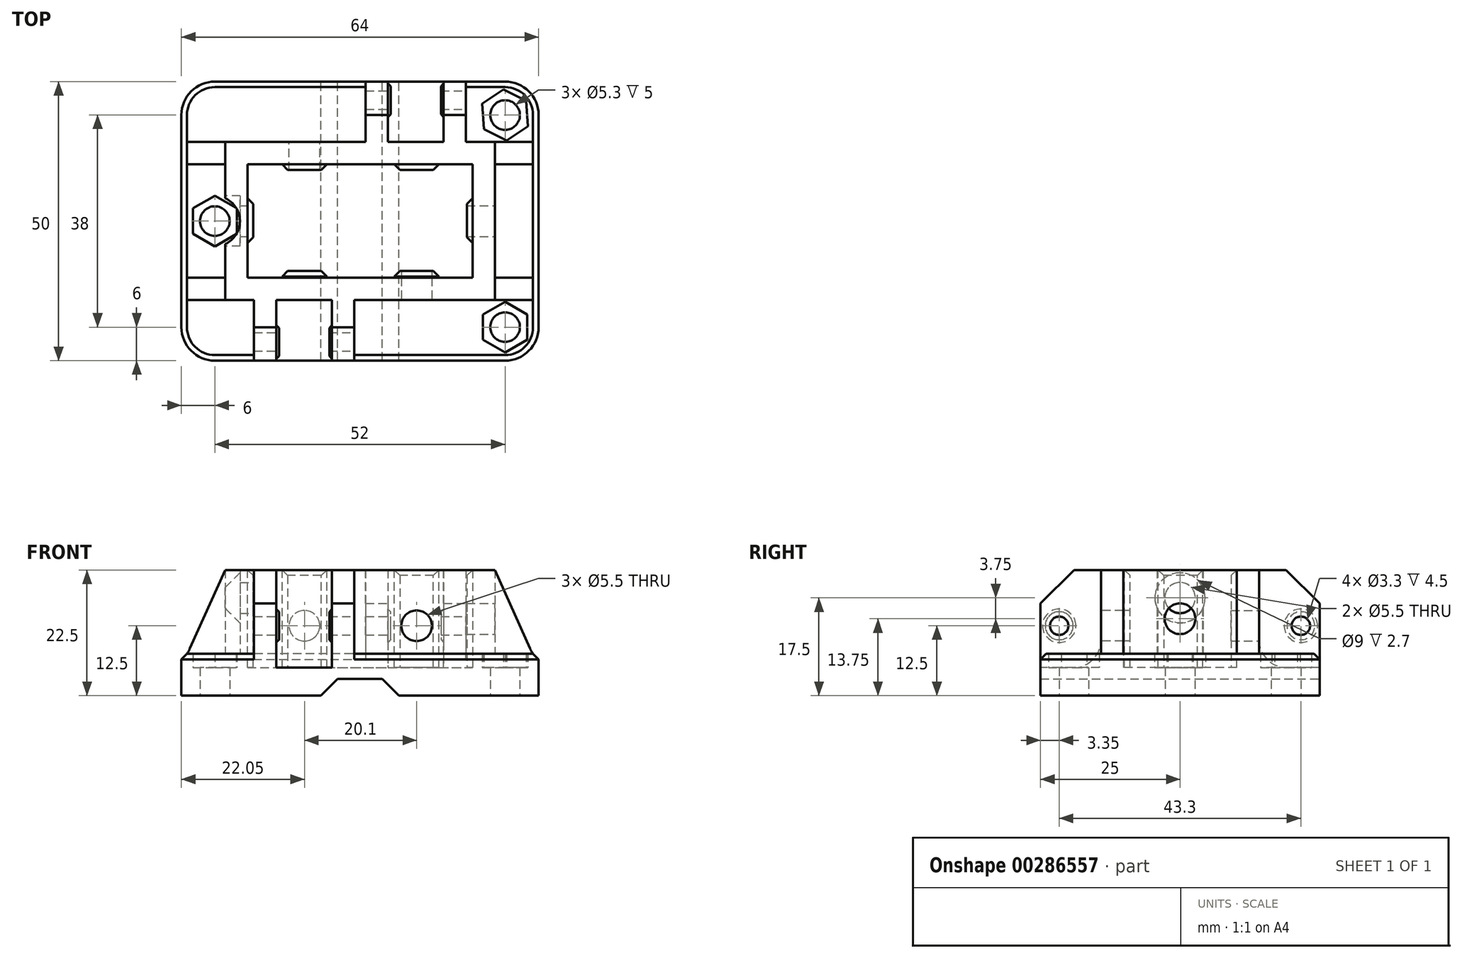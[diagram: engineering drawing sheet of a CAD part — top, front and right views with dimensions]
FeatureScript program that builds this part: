
annotation { "Feature Type Name" : "Feature", "Feature Type Description" : "" }
export const myFeature = defineFeature(function(context is Context, id is Id, definition is map)
    precondition{}
    {
        {
            var Q0;
            Q0=qCreatedBy(makeId("Top.planeOp"),FACE);
            var sketch = newSketch(context, id + "F0", { "sketchPlane" : qUnion([Q0])});
            skLineSegment(sketch, "E0.bottom", {"start": v(0, 0) * mm, "end": v(64, 0) * mm});
            skLineSegment(sketch, "E0.top", {"start": v(0, 50) * mm, "end": v(64, 50) * mm});
            skLineSegment(sketch, "E0.left", {"start": v(0, 0) * mm, "end": v(0, 50) * mm});
            skLineSegment(sketch, "E0.right", {"start": v(64, 0) * mm, "end": v(64, 50) * mm});
            skCircle(sketch, "E1", {"center": v(58, 44) * mm, "radius": 2.65 * mm});
            skPoint(sketch, "E2.centerSnap0", {"position": v(32, 0) * mm});
            skCircle(sketch, "E3", {"center": v(58, 6) * mm, "radius": 2.65 * mm});
            skCircle(sketch, "E4", {"center": v(6, 25) * mm, "radius": 2.65 * mm});
            skPoint(sketch, "E4.centerSnap0", {"position": v(0, 25) * mm});
            skSolve(sketch);
        }
        {
            var Q0;
            Q0 = qSketchRegion(id + "F0", true);
            extrude(context, id + "F1", {"entities" : qUnion([Q0]), "depth" : 5 * mm});
        }
        {
            var Q0;
            Q0=makeQuery(id+"F1.opExtrude","CAP_FACE",FACE,{"disambiguationData":[OSD([sQuery(id+"F0.wireOp",EDGE,"E0.bottom"),sQuery(id+"F0.wireOp",EDGE,"E0.top"),sQuery(id+"F0.wireOp",EDGE,"E0.left"),sQuery(id+"F0.wireOp",EDGE,"E0.right"),sQuery(id+"F0.wireOp",EDGE,"SUFVuphh-Qgx9-THfo-SX6n-8QSMb4j17lpz"),sQuery(id+"F0.wireOp",EDGE,"E1"),sQuery(id+"F0.wireOp",EDGE,"E2")])],"isStart":false});
            var sketch = newSketch(context, id + "F2", { "sketchPlane" : qUnion([Q0])});
            skLineSegment(sketch, "E5.bottom", {"start": v(7.85, 39.15) * mm, "end": v(56.15, 39.15) * mm});
            skLineSegment(sketch, "E5.top", {"start": v(7.85, 10.85) * mm, "end": v(56.15, 10.85) * mm});
            skLineSegment(sketch, "E5.left", {"start": v(7.85, 39.15) * mm, "end": v(7.85, 29.1) * mm});
            skLineSegment(sketch, "E5.right", {"start": v(56.15, 39.15) * mm, "end": v(56.15, 10.85) * mm});
            skLineSegment(sketch, "E6.0.0", {"start": v(64, 50) * mm, "end": v(0, 50) * mm, "construction": true});
            skLineSegment(sketch, "E6.0.1", {"start": v(0, 50) * mm, "end": v(0, 0) * mm, "construction": true});
            skLineSegment(sketch, "E6.0.2", {"start": v(0, 0) * mm, "end": v(64, 0) * mm, "construction": true});
            skLineSegment(sketch, "E6.0.3", {"start": v(64, 0) * mm, "end": v(64, 50) * mm, "construction": true});
            skArc(sketch, "E7", {"start": v(7.85, 20.9) * mm, "mid": v(10.5, 25) * mm, "end": v(7.85, 29.1) * mm});
            skLineSegment(sketch, "E8.trimOffspring", {"start": v(7.85, 20.9) * mm, "end": v(7.85, 10.85) * mm});
            skLineSegment(sketch, "E9.bottom", {"start": v(11.85, 35.15) * mm, "end": v(52.15, 35.15) * mm});
            skLineSegment(sketch, "E9.top", {"start": v(11.85, 14.85) * mm, "end": v(52.15, 14.85) * mm});
            skLineSegment(sketch, "E9.left", {"start": v(11.85, 35.15) * mm, "end": v(11.85, 14.85) * mm});
            skLineSegment(sketch, "E9.right", {"start": v(52.15, 35.15) * mm, "end": v(52.15, 14.85) * mm});
            skSolve(sketch);
        }
        {
            var Q0;
            Q0 = qSketchRegion(id + "F2", true);
            extrude(context, id + "F3", {"entities" : qUnion([Q0]), "operationType" : NewBodyOperationType.ADD, "depth" : 17.5 * mm});
        }
        {
            var Q0;
            Q0=makeQuery(id+"F3.opExtrude","CAP_FACE",FACE,{"disambiguationData":[OSD([sQuery(id+"F2.wireOp",EDGE,"E5.bottom"),sQuery(id+"F2.wireOp",EDGE,"E5.top"),sQuery(id+"F2.wireOp",EDGE,"E5.left"),sQuery(id+"F2.wireOp",EDGE,"E5.right"),sQuery(id+"F2.wireOp",EDGE,"E7"),sQuery(id+"F2.wireOp",EDGE,"E8.trimOffspring"),sQuery(id+"F2.wireOp",EDGE,"E9.bottom"),sQuery(id+"F2.wireOp",EDGE,"E9.top"),sQuery(id+"F2.wireOp",EDGE,"E9.left"),sQuery(id+"F2.wireOp",EDGE,"E9.right")])],"isStart":false});
            var sketch = newSketch(context, id + "F4", { "sketchPlane" : qUnion([Q0])});
            skLineSegment(sketch, "E10.bottom", {"start": v(11.85, 29.1) * mm, "end": v(12.85, 29.1) * mm});
            skLineSegment(sketch, "E10.top", {"start": v(11.85, 21.1) * mm, "end": v(12.85, 21.1) * mm});
            skLineSegment(sketch, "E10.left", {"start": v(11.85, 29.1) * mm, "end": v(11.85, 21.1) * mm});
            skLineSegment(sketch, "E10.right", {"start": v(12.85, 29.1) * mm, "end": v(12.85, 21.1) * mm});
            skLineSegment(sketch, "E11", {"start": v(32, 35.15) * mm, "end": v(32, 14.85) * mm, "construction": true});
            skLineSegment(sketch, "E12.MirrorCS", {"start": v(52.15, 29.1) * mm, "end": v(51.15, 29.1) * mm});
            skLineSegment(sketch, "E13.MirrorCS", {"start": v(52.15, 21.1) * mm, "end": v(51.15, 21.1) * mm});
            skLineSegment(sketch, "E14.MirrorCS", {"start": v(51.15, 29.1) * mm, "end": v(51.15, 21.1) * mm});
            skLineSegment(sketch, "E15.MirrorCS", {"start": v(52.15, 29.1) * mm, "end": v(52.15, 21.1) * mm});
            skLineSegment(sketch, "E16.bottom", {"start": v(38.15, 35.15) * mm, "end": v(46.15, 35.15) * mm});
            skLineSegment(sketch, "E16.top", {"start": v(38.15, 34.15) * mm, "end": v(46.15, 34.15) * mm});
            skLineSegment(sketch, "E16.left", {"start": v(38.15, 35.15) * mm, "end": v(38.15, 34.15) * mm});
            skLineSegment(sketch, "E16.right", {"start": v(46.15, 35.15) * mm, "end": v(46.15, 34.15) * mm});
            skLineSegment(sketch, "E17.bottom", {"start": v(18.05, 35.15) * mm, "end": v(26.05, 35.15) * mm});
            skLineSegment(sketch, "E17.top", {"start": v(18.05, 34.15) * mm, "end": v(26.05, 34.15) * mm});
            skLineSegment(sketch, "E17.left", {"start": v(18.05, 35.15) * mm, "end": v(18.05, 34.15) * mm});
            skLineSegment(sketch, "E17.right", {"start": v(26.05, 35.15) * mm, "end": v(26.05, 34.15) * mm});
            skLineSegment(sketch, "E18", {"start": v(52.15, 25.1) * mm, "end": v(11.85, 25.1) * mm, "construction": true});
            skLineSegment(sketch, "E19.MirrorCS", {"start": v(38.15, 15.05) * mm, "end": v(38.15, 16.05) * mm});
            skLineSegment(sketch, "E20.MirrorCS", {"start": v(18.05, 15.05) * mm, "end": v(18.05, 16.05) * mm});
            skLineSegment(sketch, "E21.MirrorCS", {"start": v(26.05, 15.05) * mm, "end": v(26.05, 16.05) * mm});
            skLineSegment(sketch, "E22.MirrorCS", {"start": v(46.15, 15.05) * mm, "end": v(46.15, 16.05) * mm});
            skLineSegment(sketch, "E23.MirrorCS", {"start": v(38.15, 15.05) * mm, "end": v(46.15, 15.05) * mm});
            skLineSegment(sketch, "E24.MirrorCS", {"start": v(18.05, 16.05) * mm, "end": v(26.05, 16.05) * mm});
            skLineSegment(sketch, "E25.MirrorCS", {"start": v(18.05, 15.05) * mm, "end": v(26.05, 15.05) * mm});
            skLineSegment(sketch, "E26.MirrorCS", {"start": v(38.15, 16.05) * mm, "end": v(46.15, 16.05) * mm});
            skSolve(sketch);
        }
        {
            var Q0;
            Q0 = qSketchRegion(id + "F4", true);
            var Q1;
            Q1=makeQuery(id+"F3.boolean.opBoolean","SPLIT",FACE,{"disambiguationData":[TD([makeQuery(id+"F3.opExtrude","SWEPT_FACE",FACE,{"disambiguationData":[OSD([sQuery(id+"F2.wireOp",EDGE,"E9.bottom")])]})])],"derivedFrom":makeQuery(id+"F1.opExtrude","CAP_FACE",FACE,{"disambiguationData":[OSD([sQuery(id+"F0.wireOp",EDGE,"E0.bottom"),sQuery(id+"F0.wireOp",EDGE,"E0.top"),sQuery(id+"F0.wireOp",EDGE,"E0.left"),sQuery(id+"F0.wireOp",EDGE,"E0.right"),sQuery(id+"F0.wireOp",EDGE,"E1"),sQuery(id+"F0.wireOp",EDGE,"E3"),sQuery(id+"F0.wireOp",EDGE,"E4")])],"isStart":false})});
            extrude(context, id + "F5", {"entities" : qUnion([Q0]), "operationType" : NewBodyOperationType.ADD, "endBound" : BoundingType.UP_TO_SURFACE, "oppositeDirection" : true, "endBoundEntityFace" : qUnion([Q1]), "depth" : 25 * mm});
        }
        {
            var Q0;
            Q0=makeQuery(id+"F5.opExtrude","SWEPT_EDGE",EDGE,{"disambiguationData":[OSD([sQuery(id+"F4.wireOp",EDGE,"E10.bottom"),sQuery(id+"F4.wireOp",EDGE,"E10.right")])]});
            var Q1;
            Q1=makeQuery(id+"F5.opExtrude","SWEPT_EDGE",EDGE,{"disambiguationData":[OSD([sQuery(id+"F4.wireOp",EDGE,"E10.top"),sQuery(id+"F4.wireOp",EDGE,"E10.right")])]});
            var Q2;
            Q2=makeQuery(id+"F5.opExtrude","CAP_EDGE",EDGE,{"disambiguationData":[OSD([sQuery(id+"F4.wireOp",EDGE,"E10.right")])],"isStart":true});
            var Q3;
            Q3=makeQuery(id+"F5.opExtrude","SWEPT_EDGE",EDGE,{"disambiguationData":[OSD([sQuery(id+"F4.wireOp",EDGE,"E12.MirrorCS"),sQuery(id+"F4.wireOp",EDGE,"E14.MirrorCS")])]});
            var Q4;
            Q4=makeQuery(id+"F5.opExtrude","SWEPT_EDGE",EDGE,{"disambiguationData":[OSD([sQuery(id+"F4.wireOp",EDGE,"E13.MirrorCS"),sQuery(id+"F4.wireOp",EDGE,"E14.MirrorCS")])]});
            var Q5;
            Q5=makeQuery(id+"F5.opExtrude","CAP_EDGE",EDGE,{"disambiguationData":[OSD([sQuery(id+"F4.wireOp",EDGE,"E14.MirrorCS")])],"isStart":true});
            var Q6;
            Q6=makeQuery(id+"F5.opExtrude","SWEPT_EDGE",EDGE,{"disambiguationData":[OSD([sQuery(id+"F4.wireOp",EDGE,"E17.top"),sQuery(id+"F4.wireOp",EDGE,"E17.left")])]});
            var Q7;
            Q7=makeQuery(id+"F5.opExtrude","CAP_EDGE",EDGE,{"disambiguationData":[OSD([sQuery(id+"F4.wireOp",EDGE,"E17.top")])],"isStart":true});
            var Q8;
            Q8=makeQuery(id+"F5.opExtrude","SWEPT_EDGE",EDGE,{"disambiguationData":[OSD([sQuery(id+"F4.wireOp",EDGE,"E17.top"),sQuery(id+"F4.wireOp",EDGE,"E17.right")])]});
            var Q9;
            Q9=makeQuery(id+"F5.opExtrude","SWEPT_EDGE",EDGE,{"disambiguationData":[OSD([sQuery(id+"F4.wireOp",EDGE,"E16.top"),sQuery(id+"F4.wireOp",EDGE,"E16.left")])]});
            var Q10;
            Q10=makeQuery(id+"F5.opExtrude","CAP_EDGE",EDGE,{"disambiguationData":[OSD([sQuery(id+"F4.wireOp",EDGE,"E16.top")])],"isStart":true});
            var Q11;
            Q11=makeQuery(id+"F5.opExtrude","SWEPT_EDGE",EDGE,{"disambiguationData":[OSD([sQuery(id+"F4.wireOp",EDGE,"E16.top"),sQuery(id+"F4.wireOp",EDGE,"E16.right")])]});
            var Q12;
            Q12=makeQuery(id+"F5.opExtrude","CAP_EDGE",EDGE,{"disambiguationData":[OSD([sQuery(id+"F4.wireOp",EDGE,"E26.MirrorCS")])],"isStart":true});
            var Q13;
            Q13=makeQuery(id+"F5.opExtrude","CAP_EDGE",EDGE,{"disambiguationData":[OSD([sQuery(id+"F4.wireOp",EDGE,"E24.MirrorCS")])],"isStart":true});
            var Q14;
            Q14=makeQuery(id+"F5.opExtrude","SWEPT_EDGE",EDGE,{"disambiguationData":[OSD([sQuery(id+"F4.wireOp",EDGE,"E20.MirrorCS"),sQuery(id+"F4.wireOp",EDGE,"E24.MirrorCS")])]});
            var Q15;
            Q15=makeQuery(id+"F5.opExtrude","SWEPT_EDGE",EDGE,{"disambiguationData":[OSD([sQuery(id+"F4.wireOp",EDGE,"E21.MirrorCS"),sQuery(id+"F4.wireOp",EDGE,"E24.MirrorCS")])]});
            var Q16;
            Q16=makeQuery(id+"F5.opExtrude","SWEPT_EDGE",EDGE,{"disambiguationData":[OSD([sQuery(id+"F4.wireOp",EDGE,"E19.MirrorCS"),sQuery(id+"F4.wireOp",EDGE,"E26.MirrorCS")])]});
            var Q17;
            Q17=makeQuery(id+"F5.opExtrude","SWEPT_EDGE",EDGE,{"disambiguationData":[OSD([sQuery(id+"F4.wireOp",EDGE,"E22.MirrorCS"),sQuery(id+"F4.wireOp",EDGE,"E26.MirrorCS")])]});
            chamfer(context, id + "F6", {"entities" : qUnion([Q0, Q1, Q2, Q3, Q4, Q5, Q6, Q7, Q8, Q9, Q10, Q11, Q12, Q13, Q14, Q15, Q16, Q17]), "width" : 1 * mm, "tangentPropagation" : true});
        }
        {
            var Q0;
            Q0=makeQuery(id+"F1.opExtrude","SWEPT_EDGE",EDGE,{"disambiguationData":[OSD([sQuery(id+"F0.wireOp",EDGE,"E0.bottom"),sQuery(id+"F0.wireOp",EDGE,"E0.right")])]});
            var Q1;
            Q1=makeQuery(id+"F1.opExtrude","SWEPT_EDGE",EDGE,{"disambiguationData":[OSD([sQuery(id+"F0.wireOp",EDGE,"E0.top"),sQuery(id+"F0.wireOp",EDGE,"E0.left")])]});
            var Q2;
            Q2=makeQuery(id+"F1.opExtrude","SWEPT_EDGE",EDGE,{"disambiguationData":[OSD([sQuery(id+"F0.wireOp",EDGE,"E0.top"),sQuery(id+"F0.wireOp",EDGE,"E0.right")])]});
            var Q3;
            Q3=makeQuery(id+"F1.opExtrude","SWEPT_EDGE",EDGE,{"disambiguationData":[OSD([sQuery(id+"F0.wireOp",EDGE,"E0.bottom"),sQuery(id+"F0.wireOp",EDGE,"E0.left")])]});
            fillet(context, id + "F7", {"entities" : qUnion([Q0, Q1, Q2, Q3]), "radius" : 6 * mm, "tangentPropagation" : true, "allowEdgeOverflow" : false});
        }
        {
            var Q0;
            {var subQ0=sQuery(id+"F0.wireOp",EDGE,"E0.left");var subQ1=sQuery(id+"F0.wireOp",EDGE,"E4");var subQ2=sQuery(id+"F0.wireOp",EDGE,"E3");var subQ3=sQuery(id+"F0.wireOp",EDGE,"E1");var subQ4=sQuery(id+"F0.wireOp",EDGE,"E0.bottom");var subQ5=sQuery(id+"F0.wireOp",EDGE,"E0.right");var subQ6=sQuery(id+"F0.wireOp",EDGE,"E0.top");Q0=makeQuery(id+"F3.boolean.opBoolean","SPLIT",FACE,{"disambiguationData":[TD([makeQuery(id+"F1.opExtrude","SWEPT_FACE",FACE,{"disambiguationData":[OSD([subQ4])]})])],"derivedFrom":makeQuery(id+"F1.opExtrude","CAP_FACE",FACE,{"disambiguationData":[OSD([subQ4,subQ6,subQ0,subQ5,subQ3,subQ2,subQ1])],"isStart":false})});}
            var sketch = newSketch(context, id + "F8", { "sketchPlane" : qUnion([Q0])});
            skLineSegment(sketch, "E27.bottom", {"start": v(7.85, 39.15) * mm, "end": v(0, 39.15) * mm});
            skLineSegment(sketch, "E27.top", {"start": v(7.85, 35.15) * mm, "end": v(0, 35.15) * mm});
            skLineSegment(sketch, "E27.left", {"start": v(7.85, 39.15) * mm, "end": v(7.85, 35.15) * mm});
            skLineSegment(sketch, "E27.right", {"start": v(0, 39.15) * mm, "end": v(0, 35.15) * mm});
            skLineSegment(sketch, "E28.bottom", {"start": v(7.85, 10.85) * mm, "end": v(0, 10.85) * mm});
            skLineSegment(sketch, "E28.top", {"start": v(7.85, 14.85) * mm, "end": v(0, 14.85) * mm});
            skLineSegment(sketch, "E28.left", {"start": v(7.85, 10.85) * mm, "end": v(7.85, 14.85) * mm});
            skLineSegment(sketch, "E28.right", {"start": v(0, 10.85) * mm, "end": v(0, 14.85) * mm});
            skLineSegment(sketch, "E29.bottom", {"start": v(56.15, 39.15) * mm, "end": v(64, 39.15) * mm});
            skLineSegment(sketch, "E29.top", {"start": v(56.15, 35.15) * mm, "end": v(64, 35.15) * mm});
            skLineSegment(sketch, "E29.left", {"start": v(56.15, 39.15) * mm, "end": v(56.15, 35.15) * mm});
            skLineSegment(sketch, "E29.right", {"start": v(64, 39.15) * mm, "end": v(64, 35.15) * mm});
            skLineSegment(sketch, "E30.bottom", {"start": v(56.15, 10.85) * mm, "end": v(64, 10.85) * mm});
            skLineSegment(sketch, "E30.top", {"start": v(56.15, 14.85) * mm, "end": v(64, 14.85) * mm});
            skLineSegment(sketch, "E30.left", {"start": v(56.15, 10.85) * mm, "end": v(56.15, 14.85) * mm});
            skLineSegment(sketch, "E30.right", {"start": v(64, 10.85) * mm, "end": v(64, 14.85) * mm});
            skLineSegment(sketch, "E31.bottom", {"start": v(7.85, 10.85) * mm, "end": v(12.5, 10.85) * mm});
            skLineSegment(sketch, "E32.bottom", {"start": v(7.85, 39.15) * mm, "end": v(12.5, 39.15) * mm});
            skLineSegment(sketch, "E33.0.0", {"start": v(7.85, 20.9) * mm, "end": v(7.85, 10.85) * mm, "construction": true});
            skLineSegment(sketch, "E33.0.1", {"start": v(12.5, 10.85) * mm, "end": v(48.25, 10.85) * mm, "construction": true});
            skLineSegment(sketch, "E33.0.2", {"start": v(56.15, 10.85) * mm, "end": v(56.15, 39.15) * mm, "construction": true});
            skLineSegment(sketch, "E33.0.3", {"start": v(56.15, 39.15) * mm, "end": v(12.5, 39.15) * mm, "construction": true});
            skLineSegment(sketch, "E33.0.4", {"start": v(7.85, 39.15) * mm, "end": v(7.85, 29.1) * mm, "construction": true});
            skArc(sketch, "E33.0.5", {"start": v(7.85, 29.1) * mm, "mid": v(10.5, 25) * mm, "end": v(7.85, 20.9) * mm, "construction": true});
            skLineSegment(sketch, "E34.0", {"start": v(52.15, 35.15) * mm, "end": v(52.15, 29.1) * mm, "construction": true});
            skLineSegment(sketch, "E35.0", {"start": v(52.15, 21.1) * mm, "end": v(52.15, 14.85) * mm, "construction": true});
            skLineSegment(sketch, "E36.bottom", {"start": v(51, 39.15) * mm, "end": v(47, 39.15) * mm});
            skLineSegment(sketch, "E36.top", {"start": v(51, 50) * mm, "end": v(47, 50) * mm});
            skLineSegment(sketch, "E36.left", {"start": v(51, 39.15) * mm, "end": v(51, 50) * mm});
            skLineSegment(sketch, "E36.right", {"start": v(47, 39.15) * mm, "end": v(47, 50) * mm});
            skLineSegment(sketch, "E37.bottom", {"start": v(37, 50) * mm, "end": v(33, 50) * mm});
            skLineSegment(sketch, "E37.top", {"start": v(37, 39.15) * mm, "end": v(33, 39.15) * mm});
            skLineSegment(sketch, "E37.left", {"start": v(37, 50) * mm, "end": v(37, 39.15) * mm});
            skLineSegment(sketch, "E37.right", {"start": v(33, 50) * mm, "end": v(33, 39.15) * mm});
            skLineSegment(sketch, "E38.bottom", {"start": v(27, 10.85) * mm, "end": v(31, 10.85) * mm});
            skLineSegment(sketch, "E38.top", {"start": v(27, 0) * mm, "end": v(31, 0) * mm});
            skLineSegment(sketch, "E38.left", {"start": v(27, 10.85) * mm, "end": v(27, 0) * mm});
            skLineSegment(sketch, "E38.right", {"start": v(31, 10.85) * mm, "end": v(31, 0) * mm});
            skLineSegment(sketch, "E39.bottom", {"start": v(17, 10.85) * mm, "end": v(13, 10.85) * mm});
            skLineSegment(sketch, "E39.top", {"start": v(17, 0) * mm, "end": v(13, 0) * mm});
            skLineSegment(sketch, "E39.left", {"start": v(17, 10.85) * mm, "end": v(17, 0) * mm});
            skLineSegment(sketch, "E39.right", {"start": v(13, 10.85) * mm, "end": v(13, 0) * mm});
            skLineSegment(sketch, "E40.trimOffspring", {"start": v(52.15, 10.85) * mm, "end": v(56.15, 10.85) * mm, "construction": true});
            skSolve(sketch);
        }
        {
            var Q0;
            Q0 = qSketchRegion(id + "F8", true);
            var Q1;
            Q1=makeQuery(id+"F5.boolean.opBoolean","MERGE",FACE,{"derivedFrom":[makeQuery(id+"F3.opExtrude","CAP_FACE",FACE,{"disambiguationData":[OSD([sQuery(id+"F2.wireOp",EDGE,"E5.bottom"),sQuery(id+"F2.wireOp",EDGE,"E5.top"),sQuery(id+"F2.wireOp",EDGE,"E5.left"),sQuery(id+"F2.wireOp",EDGE,"E5.right"),sQuery(id+"F2.wireOp",EDGE,"E7"),sQuery(id+"F2.wireOp",EDGE,"E8.trimOffspring"),sQuery(id+"F2.wireOp",EDGE,"E9.bottom"),sQuery(id+"F2.wireOp",EDGE,"E9.top"),sQuery(id+"F2.wireOp",EDGE,"E9.left"),sQuery(id+"F2.wireOp",EDGE,"E9.right")])],"isStart":false}),makeQuery(id+"F5.opExtrude","CAP_FACE",FACE,{"disambiguationData":[OSD([sQuery(id+"F4.wireOp",EDGE,"E10.bottom"),sQuery(id+"F4.wireOp",EDGE,"E10.top"),sQuery(id+"F4.wireOp",EDGE,"E10.left"),sQuery(id+"F4.wireOp",EDGE,"E10.right")])],"isStart":true}),makeQuery(id+"F5.opExtrude","CAP_FACE",FACE,{"disambiguationData":[OSD([sQuery(id+"F4.wireOp",EDGE,"E12.MirrorCS"),sQuery(id+"F4.wireOp",EDGE,"E13.MirrorCS"),sQuery(id+"F4.wireOp",EDGE,"E14.MirrorCS"),sQuery(id+"F4.wireOp",EDGE,"E15.MirrorCS")])],"isStart":true}),makeQuery(id+"F5.opExtrude","CAP_FACE",FACE,{"disambiguationData":[OSD([sQuery(id+"F4.wireOp",EDGE,"E16.bottom"),sQuery(id+"F4.wireOp",EDGE,"E16.top"),sQuery(id+"F4.wireOp",EDGE,"E16.left"),sQuery(id+"F4.wireOp",EDGE,"E16.right")])],"isStart":true}),makeQuery(id+"F5.opExtrude","CAP_FACE",FACE,{"disambiguationData":[OSD([sQuery(id+"F4.wireOp",EDGE,"E17.bottom"),sQuery(id+"F4.wireOp",EDGE,"E17.top"),sQuery(id+"F4.wireOp",EDGE,"E17.left"),sQuery(id+"F4.wireOp",EDGE,"E17.right")])],"isStart":true})]});
            extrude(context, id + "F9", {"entities" : qUnion([Q0]), "operationType" : NewBodyOperationType.ADD, "endBound" : BoundingType.UP_TO_SURFACE, "endBoundEntityFace" : qUnion([Q1]), "depth" : 25 * mm});
        }
        {
            var Q0;
            {var subQ0=makeQuery(id+"F9.opExtrude","SWEPT_FACE",FACE,{"disambiguationData":[OSD([sQuery(id+"F8.wireOp",EDGE,"E30.bottom")])]});var subQ1=makeQuery(id+"F9.opExtrude","SWEPT_FACE",FACE,{"disambiguationData":[OSD([sQuery(id+"F8.wireOp",EDGE,"E28.bottom")])]});var subQ2=makeQuery(id+"F3.opExtrude","SWEPT_FACE",FACE,{"disambiguationData":[OSD([sQuery(id+"F2.wireOp",EDGE,"E5.top")])]});Q0=qUnion([makeQuery(id+"F9.boolean.opBoolean","MERGE",FACE,{"disambiguationData":[OD(2.0)],"derivedFrom":[subQ2,subQ1,subQ0]}),makeQuery(id+"F9.boolean.opBoolean","MERGE",FACE,{"disambiguationData":[OD(0.0)],"derivedFrom":[subQ2,subQ1,subQ0]}),makeQuery(id+"F9.boolean.opBoolean","MERGE",FACE,{"disambiguationData":[OD(1.0)],"derivedFrom":[subQ2,subQ1,subQ0]})]);}
            var sketch = newSketch(context, id + "F10", { "sketchPlane" : qUnion([Q0])});
            skLineSegment(sketch, "E41", {"start": v(0, 5) * mm, "end": v(0, 22.5) * mm});
            skLineSegment(sketch, "E42.0.0", {"start": v(64, 22.5) * mm, "end": v(56.15, 22.5) * mm, "construction": true});
            skLineSegment(sketch, "E42.0.1", {"start": v(56.15, 22.5) * mm, "end": v(56.15, 5) * mm, "construction": true});
            skLineSegment(sketch, "E42.0.2", {"start": v(56.15, 5) * mm, "end": v(64, 5) * mm, "construction": true});
            skLineSegment(sketch, "E42.0.3", {"start": v(64, 5) * mm, "end": v(64, 22.5) * mm});
            skLineSegment(sketch, "E43", {"start": v(56.15, 22.5) * mm, "end": v(64, 22.5) * mm});
            skLineSegment(sketch, "E44", {"start": v(64, 5) * mm, "end": v(56.15, 22.5) * mm});
            skLineSegment(sketch, "E45.0.1", {"start": v(7.85, 22.5) * mm, "end": v(7.85, 5) * mm, "construction": true});
            skLineSegment(sketch, "E45.0.3", {"start": v(7.85, 5) * mm, "end": v(7.85, 22.5) * mm, "construction": true});
            skLineSegment(sketch, "E46", {"start": v(0, 22.5) * mm, "end": v(7.85, 22.5) * mm});
            skLineSegment(sketch, "E47", {"start": v(0, 5) * mm, "end": v(7.85, 22.5) * mm});
            skSolve(sketch);
        }
        {
            var Q0;
            Q0 = qSketchRegion(id + "F10", true);
            var Q1;
            {var subQ0=makeQuery(id+"F9.opExtrude","SWEPT_FACE",FACE,{"disambiguationData":[OSD([sQuery(id+"F8.wireOp",EDGE,"E29.bottom")])]});var subQ1=makeQuery(id+"F9.opExtrude","SWEPT_FACE",FACE,{"disambiguationData":[OSD([sQuery(id+"F8.wireOp",EDGE,"E27.bottom")])]});var subQ2=makeQuery(id+"F3.opExtrude","SWEPT_FACE",FACE,{"disambiguationData":[OSD([sQuery(id+"F2.wireOp",EDGE,"E5.bottom")])]});Q1=qUnion([makeQuery(id+"F9.boolean.opBoolean","MERGE",FACE,{"disambiguationData":[OD(1.0)],"derivedFrom":[subQ2,subQ1,subQ0]}),makeQuery(id+"F9.boolean.opBoolean","MERGE",FACE,{"disambiguationData":[OD(2.0)],"derivedFrom":[subQ2,subQ1,subQ0]}),makeQuery(id+"F9.boolean.opBoolean","MERGE",FACE,{"disambiguationData":[OD(0.0)],"derivedFrom":[subQ2,subQ1,subQ0]})]);}
            extrude(context, id + "F11", {"entities" : qUnion([Q0]), "operationType" : NewBodyOperationType.REMOVE, "endBound" : BoundingType.UP_TO_SURFACE, "oppositeDirection" : true, "endBoundEntityFace" : qUnion([Q1]), "depth" : 25 * mm});
        }
        {
            var Q0;
            Q0=makeQuery(id+"F3.opExtrude","SWEPT_FACE",FACE,{"disambiguationData":[OSD([sQuery(id+"F2.wireOp",EDGE,"E5.right")])]});
            var sketch = newSketch(context, id + "F12", { "sketchPlane" : qUnion([Q0])});
            skCircle(sketch, "E48", {"center": v(25, 13.75) * mm, "radius": 2.75 * mm});
            skPoint(sketch, "E48.centerSnap0", {"position": v(35.15, 13.75) * mm});
            skPoint(sketch, "E48.centerSnap1", {"position": v(25, 22.5) * mm});
            skSolve(sketch);
        }
        {
            var Q0;
            Q0 = qSketchRegion(id + "F12", true);
            var Q1;
            Q1=makeQuery(id+"F5.opExtrude","SWEPT_FACE",FACE,{"disambiguationData":[OSD([sQuery(id+"F4.wireOp",EDGE,"E14.MirrorCS")])]});
            extrude(context, id + "F13", {"entities" : qUnion([Q0]), "operationType" : NewBodyOperationType.REMOVE, "endBound" : BoundingType.UP_TO_SURFACE, "oppositeDirection" : true, "endBoundEntityFace" : qUnion([Q1]), "depth" : 25 * mm});
        }
        {
            var Q0;
            Q0=makeQuery(id+"F9.boolean.opBoolean","MERGE",FACE,{"disambiguationData":[OD(1.0)],"derivedFrom":[makeQuery(id+"F3.opExtrude","SWEPT_FACE",FACE,{"disambiguationData":[OSD([sQuery(id+"F2.wireOp",EDGE,"E5.bottom")])]}),makeQuery(id+"F9.opExtrude","SWEPT_FACE",FACE,{"disambiguationData":[OSD([sQuery(id+"F8.wireOp",EDGE,"E27.bottom")])]}),makeQuery(id+"F9.opExtrude","SWEPT_FACE",FACE,{"disambiguationData":[OSD([sQuery(id+"F8.wireOp",EDGE,"E29.bottom")])]})]});
            var sketch = newSketch(context, id + "F14", { "sketchPlane" : qUnion([Q0])});
            skCircle(sketch, "E49", {"center": v(-42.15, 12.5) * mm, "radius": 2.75 * mm, "construction": true});
            skPoint(sketch, "E49.centerSnap0", {"position": v(-47.15, 12.5) * mm});
            skLineSegment(sketch, "E50.0.0", {"start": v(-39.15, 5) * mm, "end": v(-45.15, 5) * mm, "construction": true});
            skLineSegment(sketch, "E50.0.1", {"start": v(-45.15, 5) * mm, "end": v(-45.15, 21.5) * mm, "construction": true});
            skLineSegment(sketch, "E50.0.2", {"start": v(-45.15, 21.5) * mm, "end": v(-39.15, 21.5) * mm, "construction": true});
            skLineSegment(sketch, "E50.0.3", {"start": v(-39.15, 21.5) * mm, "end": v(-39.15, 5) * mm, "construction": true});
            skLineSegment(sketch, "E51.0.0", {"start": v(-19.05, 5) * mm, "end": v(-25.05, 5) * mm, "construction": true});
            skLineSegment(sketch, "E51.0.1", {"start": v(-25.05, 5) * mm, "end": v(-25.05, 21.5) * mm, "construction": true});
            skLineSegment(sketch, "E51.0.2", {"start": v(-25.05, 21.5) * mm, "end": v(-19.05, 21.5) * mm, "construction": true});
            skLineSegment(sketch, "E51.0.3", {"start": v(-19.05, 21.5) * mm, "end": v(-19.05, 5) * mm, "construction": true});
            skCircle(sketch, "E52", {"center": v(-22.05, 12.5) * mm, "radius": 2.75 * mm});
            skPoint(sketch, "E52.centerSnap0", {"position": v(-22.05, 21.5) * mm});
            skSolve(sketch);
        }
        {
            var Q0;
            Q0 = qSketchRegion(id + "F14", true);
            var Q1;
            Q1=makeQuery(id+"F5.opExtrude","SWEPT_FACE",FACE,{"disambiguationData":[OSD([sQuery(id+"F4.wireOp",EDGE,"E17.top")])]});
            extrude(context, id + "F15", {"entities" : qUnion([Q0]), "operationType" : NewBodyOperationType.REMOVE, "endBound" : BoundingType.UP_TO_SURFACE, "oppositeDirection" : true, "endBoundEntityFace" : qUnion([Q1]), "depth" : 25 * mm});
        }
        {
            var Q0;
            Q0=makeQuery(id+"F9.opExtrude","SWEPT_FACE",FACE,{"disambiguationData":[OSD([sQuery(id+"F8.wireOp",EDGE,"E36.left")])]});
            var sketch = newSketch(context, id + "F16", { "sketchPlane" : qUnion([Q0])});
            skCircle(sketch, "E53", {"center": v(46.65, 12.5) * mm, "radius": 1.65 * mm});
            skLineSegment(sketch, "E54.0.0", {"start": v(35.15, 22.5) * mm, "end": v(14.85, 22.5) * mm, "construction": true});
            skLineSegment(sketch, "E54.0.1", {"start": v(14.85, 22.5) * mm, "end": v(14.85, 5) * mm, "construction": true});
            skLineSegment(sketch, "E54.0.2", {"start": v(14.85, 5) * mm, "end": v(35.15, 5) * mm, "construction": true});
            skLineSegment(sketch, "E54.0.3", {"start": v(35.15, 5) * mm, "end": v(35.15, 22.5) * mm, "construction": true});
            skLineSegment(sketch, "E55", {"start": v(25, 22.5) * mm, "end": v(25, 5) * mm, "construction": true});
            skCircle(sketch, "E56.MirrorC", {"center": v(3.35, 12.5) * mm, "radius": 1.65 * mm});
            skSolve(sketch);
        }
        {
            var Q0;
            Q0 = qSketchRegion(id + "F16", true);
            extrude(context, id + "F17", {"entities" : qUnion([Q0]), "operationType" : NewBodyOperationType.REMOVE, "endBound" : BoundingType.THROUGH_ALL, "oppositeDirection" : true, "depth" : 25 * mm});
        }
        {
            var Q0;
            Q0=makeQuery(id+"F9.opExtrude","CAP_EDGE",EDGE,{"disambiguationData":[OSD([sQuery(id+"F8.wireOp",EDGE,"E36.top")])],"isStart":false});
            var Q1;
            Q1=makeQuery(id+"F9.opExtrude","CAP_EDGE",EDGE,{"disambiguationData":[OSD([sQuery(id+"F8.wireOp",EDGE,"E37.bottom")])],"isStart":false});
            var Q2;
            Q2=makeQuery(id+"F9.opExtrude","CAP_EDGE",EDGE,{"disambiguationData":[OSD([sQuery(id+"F8.wireOp",EDGE,"E39.top")])],"isStart":false});
            var Q3;
            Q3=makeQuery(id+"F9.opExtrude","CAP_EDGE",EDGE,{"disambiguationData":[OSD([sQuery(id+"F8.wireOp",EDGE,"E38.top")])],"isStart":false});
            chamfer(context, id + "F18", {"entities" : qUnion([Q0, Q1, Q2, Q3]), "width" : 6 * mm, "tangentPropagation" : true});
        }
        {
            var Q0;
            Q0=makeQuery(id+"F3.opExtrude","SWEPT_FACE",FACE,{"disambiguationData":[OSD([sQuery(id+"F2.wireOp",EDGE,"E5.left")])]});
            var sketch = newSketch(context, id + "F19", { "sketchPlane" : qUnion([Q0])});
            skCircle(sketch, "E57", {"center": v(-25, 17.5) * mm, "radius": 4.5 * mm});
            skSolve(sketch);
        }
        {
            var Q0;
            Q0 = qSketchRegion(id + "F19", true);
            extrude(context, id + "F20", {"entities" : qUnion([Q0]), "operationType" : NewBodyOperationType.REMOVE, "oppositeDirection" : true, "depth" : 2.7 * mm});
        }
        {
            var Q0;
            Q0=makeQuery(id+"F9.boolean.opBoolean","MERGE",FACE,{"disambiguationData":[OD(1.0)],"derivedFrom":[makeQuery(id+"F3.opExtrude","SWEPT_FACE",FACE,{"disambiguationData":[OSD([sQuery(id+"F2.wireOp",EDGE,"E5.top")])]}),makeQuery(id+"F9.opExtrude","SWEPT_FACE",FACE,{"disambiguationData":[OSD([sQuery(id+"F8.wireOp",EDGE,"E28.bottom")])]}),makeQuery(id+"F9.opExtrude","SWEPT_FACE",FACE,{"disambiguationData":[OSD([sQuery(id+"F8.wireOp",EDGE,"E30.bottom")])]})]});
            var sketch = newSketch(context, id + "F21", { "sketchPlane" : qUnion([Q0])});
            skLineSegment(sketch, "E58.0.3", {"start": v(31, 22.5) * mm, "end": v(56.15, 22.5) * mm, "construction": true});
            skLineSegment(sketch, "E59.0.0", {"start": v(39.15, 21.5) * mm, "end": v(45.15, 21.5) * mm, "construction": true});
            skLineSegment(sketch, "E59.0.1", {"start": v(45.15, 21.5) * mm, "end": v(45.15, 5) * mm, "construction": true});
            skLineSegment(sketch, "E59.0.2", {"start": v(45.15, 5) * mm, "end": v(39.15, 5) * mm, "construction": true});
            skLineSegment(sketch, "E59.0.3", {"start": v(39.15, 5) * mm, "end": v(39.15, 21.5) * mm, "construction": true});
            skCircle(sketch, "E60", {"center": v(42.15, 12.5) * mm, "radius": 2.75 * mm});
            skPoint(sketch, "E60.centerSnap0", {"position": v(42.15, 21.5) * mm});
            skSolve(sketch);
        }
        {
            var Q0;
            Q0 = qSketchRegion(id + "F21", true);
            var Q1;
            Q1=makeQuery(id+"F5.opExtrude","SWEPT_FACE",FACE,{"disambiguationData":[OSD([sQuery(id+"F4.wireOp",EDGE,"E26.MirrorCS")])]});
            extrude(context, id + "F22", {"entities" : qUnion([Q0]), "operationType" : NewBodyOperationType.REMOVE, "endBound" : BoundingType.UP_TO_SURFACE, "oppositeDirection" : true, "endBoundEntityFace" : qUnion([Q1]), "depth" : 25 * mm});
        }
        {
            var Q0;
            Q0=makeQuery(id+"F9.opExtrude","SWEPT_FACE",FACE,{"disambiguationData":[OSD([sQuery(id+"F8.wireOp",EDGE,"E36.right")])]});
            var sketch = newSketch(context, id + "F23", { "sketchPlane" : qUnion([Q0])});
            skCircle(sketch, "E61.0", {"center": v(-46.65, 12.5) * mm, "radius": 1.65 * mm});
            skCircle(sketch, "E62", {"center": v(-46.65, 12.5) * mm, "radius": 3 * mm});
            skSolve(sketch);
        }
        {
            var Q0;
            Q0 = qSketchRegion(id + "F23", true);
            extrude(context, id + "F24", {"entities" : qUnion([Q0]), "operationType" : NewBodyOperationType.ADD, "depth" : .5 * mm});
        }
        {
            var Q0;
            Q0=makeQuery(id+"F9.opExtrude","SWEPT_FACE",FACE,{"disambiguationData":[OSD([sQuery(id+"F8.wireOp",EDGE,"E37.left")])]});
            var sketch = newSketch(context, id + "F25", { "sketchPlane" : qUnion([Q0])});
            skCircle(sketch, "E63.0", {"center": v(46.65, 12.5) * mm, "radius": 1.65 * mm});
            skCircle(sketch, "E64", {"center": v(46.65, 12.5) * mm, "radius": 3 * mm});
            skSolve(sketch);
        }
        {
            var Q0;
            Q0 = qSketchRegion(id + "F25", true);
            extrude(context, id + "F26", {"entities" : qUnion([Q0]), "operationType" : NewBodyOperationType.ADD, "depth" : .5 * mm});
        }
        {
            var Q0;
            Q0=makeQuery(id+"F9.opExtrude","SWEPT_FACE",FACE,{"disambiguationData":[OSD([sQuery(id+"F8.wireOp",EDGE,"E38.left")])]});
            var sketch = newSketch(context, id + "F27", { "sketchPlane" : qUnion([Q0])});
            skCircle(sketch, "E65", {"center": v(-3.35, 12.5) * mm, "radius": 3 * mm});
            skCircle(sketch, "E66.0", {"center": v(-3.35, 12.5) * mm, "radius": 1.65 * mm});
            skSolve(sketch);
        }
        {
            var Q0;
            Q0 = qSketchRegion(id + "F27", true);
            extrude(context, id + "F28", {"entities" : qUnion([Q0]), "operationType" : NewBodyOperationType.ADD, "depth" : .5 * mm});
        }
        {
            var Q0;
            Q0=makeQuery(id+"F9.opExtrude","SWEPT_FACE",FACE,{"disambiguationData":[OSD([sQuery(id+"F8.wireOp",EDGE,"E39.left")])]});
            var sketch = newSketch(context, id + "F29", { "sketchPlane" : qUnion([Q0])});
            skCircle(sketch, "E67.0", {"center": v(3.35, 12.5) * mm, "radius": 1.65 * mm});
            skCircle(sketch, "E68", {"center": v(3.35, 12.5) * mm, "radius": 3 * mm});
            skSolve(sketch);
        }
        {
            var Q0;
            Q0 = qSketchRegion(id + "F29", true);
            extrude(context, id + "F30", {"entities" : qUnion([Q0]), "operationType" : NewBodyOperationType.ADD, "depth" : .5 * mm});
        }
        {
            var Q0;
            Q0=makeQuery(id+"F30.opExtrude","CAP_EDGE",EDGE,{"disambiguationData":[OSD([sQuery(id+"F29.wireOp",EDGE,"E68")])],"isStart":false});
            var Q1;
            Q1=makeQuery(id+"F28.opExtrude","CAP_EDGE",EDGE,{"disambiguationData":[OSD([sQuery(id+"F27.wireOp",EDGE,"E65")])],"isStart":false});
            var Q2;
            Q2=makeQuery(id+"F26.opExtrude","CAP_EDGE",EDGE,{"disambiguationData":[OSD([sQuery(id+"F25.wireOp",EDGE,"E64")])],"isStart":false});
            var Q3;
            Q3=makeQuery(id+"F24.opExtrude","CAP_EDGE",EDGE,{"disambiguationData":[OSD([sQuery(id+"F23.wireOp",EDGE,"E62")])],"isStart":false});
            chamfer(context, id + "F31", {"entities" : qUnion([Q0, Q1, Q2, Q3]), "width" : .5 * mm, "tangentPropagation" : true});
        }
        {
            var Q0;
            Q0=makeQuery(id+"F9.boolean.opBoolean","MERGE",FACE,{"derivedFrom":[makeQuery(id+"F1.opExtrude","SWEPT_FACE",FACE,{"disambiguationData":[OSD([sQuery(id+"F0.wireOp",EDGE,"E0.top")])]}),makeQuery(id+"F9.opExtrude","SWEPT_FACE",FACE,{"disambiguationData":[OSD([sQuery(id+"F8.wireOp",EDGE,"E36.top")])]}),makeQuery(id+"F9.opExtrude","SWEPT_FACE",FACE,{"disambiguationData":[OSD([sQuery(id+"F8.wireOp",EDGE,"E37.bottom")])]})]});
            var sketch = newSketch(context, id + "F32", { "sketchPlane" : qUnion([Q0])});
            skLineSegment(sketch, "E69", {"start": v(-39, 0) * mm, "end": v(-36, 3) * mm});
            skLineSegment(sketch, "E70", {"start": v(-36, 3) * mm, "end": v(-28, 3) * mm});
            skLineSegment(sketch, "E71", {"start": v(-28, 3) * mm, "end": v(-25, 0) * mm});
            skLineSegment(sketch, "E72", {"start": v(-39, 0) * mm, "end": v(-25, 0) * mm});
            skSolve(sketch);
        }
        {
            var Q0;
            Q0 = qSketchRegion(id + "F32", true);
            extrude(context, id + "F33", {"entities" : qUnion([Q0]), "operationType" : NewBodyOperationType.REMOVE, "endBound" : BoundingType.THROUGH_ALL, "oppositeDirection" : true, "depth" : 25 * mm});
        }
        {
            var Q0;
            Q0=makeQuery(id+"F5.opExtrude","SWEPT_FACE",FACE,{"disambiguationData":[OSD([sQuery(id+"F4.wireOp",EDGE,"E10.right")])]});
            var sketch = newSketch(context, id + "F34", { "sketchPlane" : qUnion([Q0])});
            skLineSegment(sketch, "E73.0", {"start": v(29.1, 19.35) * mm, "end": v(29.1, 19.35) * mm});
            skCircle(sketch, "E74", {"center": v(25, 17.5) * mm, "radius": 2.75 * mm});
            skSolve(sketch);
        }
        {
            var Q0;
            Q0 = qSketchRegion(id + "F34", true);
            var Q1;
            Q1=makeQuery(id+"F3.opExtrude","SWEPT_FACE",FACE,{"disambiguationData":[OSD([sQuery(id+"F2.wireOp",EDGE,"E5.left")])]});
            extrude(context, id + "F35", {"entities" : qUnion([Q0]), "operationType" : NewBodyOperationType.REMOVE, "endBound" : BoundingType.UP_TO_SURFACE, "oppositeDirection" : true, "endBoundEntityFace" : qUnion([Q1]), "depth" : 25 * mm});
        }
        {
            var Q0;
            {var subQ0=sQuery(id+"F0.wireOp",EDGE,"E1");var subQ1=makeQuery(id+"F1.opExtrude","SWEPT_FACE",FACE,{"disambiguationData":[OSD([subQ0])]});var subQ2=sQuery(id+"F0.wireOp",EDGE,"E0.right");var subQ3=sQuery(id+"F0.wireOp",EDGE,"E0.top");var subQ7=sQuery(id+"F0.wireOp",EDGE,"E0.left");var subQ8=sQuery(id+"F0.wireOp",EDGE,"E4");var subQ9=sQuery(id+"F0.wireOp",EDGE,"E3");var subQ10=sQuery(id+"F0.wireOp",EDGE,"E0.bottom");Q0=makeQuery(id+"F9.boolean.opBoolean","SPLIT",FACE,{"disambiguationData":[TD([subQ1])],"derivedFrom":makeQuery(id+"F3.boolean.opBoolean","SPLIT",FACE,{"disambiguationData":[TD([makeQuery(id+"F1.opExtrude","SWEPT_FACE",FACE,{"disambiguationData":[OSD([subQ10])]})])],"derivedFrom":makeQuery(id+"F1.opExtrude","CAP_FACE",FACE,{"disambiguationData":[OSD([subQ10,subQ3,subQ7,subQ2,subQ0,subQ9,subQ8])],"isStart":false})})});}
            var sketch = newSketch(context, id + "F36", { "sketchPlane" : qUnion([Q0])});
            skCircle(sketch, "E75.0", {"center": v(58, 44) * mm, "radius": 2.65 * mm, "construction": true});
            skCircle(sketch, "E76.0", {"center": v(58, 6) * mm, "radius": 2.65 * mm, "construction": true});
            skCircle(sketch, "E77.cCircle", {"center": v(58, 44) * mm, "radius": 3.95 * mm, "construction": true});
            skLineSegment(sketch, "E77.0", {"start": v(61.8, 46.53) * mm, "end": v(62.09, 41.97) * mm});
            skLineSegment(sketch, "E77.1", {"start": v(62.09, 41.97) * mm, "end": v(58.29, 39.45) * mm});
            skLineSegment(sketch, "E77.2", {"start": v(58.29, 39.45) * mm, "end": v(54.2, 41.47) * mm});
            skLineSegment(sketch, "E77.3", {"start": v(54.2, 41.47) * mm, "end": v(53.91, 46.03) * mm});
            skLineSegment(sketch, "E77.4", {"start": v(53.91, 46.03) * mm, "end": v(57.71, 48.55) * mm});
            skLineSegment(sketch, "E77.5", {"start": v(57.71, 48.55) * mm, "end": v(61.8, 46.53) * mm});
            skPoint(sketch, "E77.0.midPoint", {"position": v(61.94, 44.25) * mm});
            skCircle(sketch, "E78.cCircle", {"center": v(58, 6) * mm, "radius": 4.09 * mm, "construction": true});
            skLineSegment(sketch, "E78.0", {"start": v(62.09, 8.36) * mm, "end": v(62.09, 3.64) * mm});
            skLineSegment(sketch, "E78.1", {"start": v(62.09, 3.64) * mm, "end": v(58, 1.28) * mm});
            skLineSegment(sketch, "E78.2", {"start": v(58, 1.28) * mm, "end": v(53.91, 3.64) * mm});
            skLineSegment(sketch, "E78.3", {"start": v(53.91, 3.64) * mm, "end": v(53.91, 8.36) * mm});
            skLineSegment(sketch, "E78.4", {"start": v(53.91, 8.36) * mm, "end": v(58, 10.72) * mm});
            skLineSegment(sketch, "E78.5", {"start": v(58, 10.72) * mm, "end": v(62.09, 8.36) * mm});
            skPoint(sketch, "E78.0.midPoint", {"position": v(62.09, 6) * mm});
            skSolve(sketch);
        }
        {
            var Q0;
            {var subQ1=sQuery(id+"F0.wireOp",EDGE,"E4");var subQ2=makeQuery(id+"F1.opExtrude","SWEPT_FACE",FACE,{"disambiguationData":[OSD([subQ1])]});var subQ5=sQuery(id+"F0.wireOp",EDGE,"E0.left");var subQ7=sQuery(id+"F0.wireOp",EDGE,"E3");var subQ8=sQuery(id+"F0.wireOp",EDGE,"E1");var subQ9=sQuery(id+"F0.wireOp",EDGE,"E0.bottom");var subQ10=sQuery(id+"F0.wireOp",EDGE,"E0.right");var subQ11=sQuery(id+"F0.wireOp",EDGE,"E0.top");Q0=makeQuery(id+"F9.boolean.opBoolean","SPLIT",FACE,{"disambiguationData":[TD([subQ2])],"derivedFrom":makeQuery(id+"F3.boolean.opBoolean","SPLIT",FACE,{"disambiguationData":[TD([makeQuery(id+"F1.opExtrude","SWEPT_FACE",FACE,{"disambiguationData":[OSD([subQ9])]})])],"derivedFrom":makeQuery(id+"F1.opExtrude","CAP_FACE",FACE,{"disambiguationData":[OSD([subQ9,subQ11,subQ5,subQ10,subQ8,subQ7,subQ1])],"isStart":false})})});}
            var sketch = newSketch(context, id + "F37", { "sketchPlane" : qUnion([Q0])});
            skCircle(sketch, "E79.0", {"center": v(6, 25) * mm, "radius": 2.65 * mm, "construction": true});
            skCircle(sketch, "E80.cCircle", {"center": v(6, 25) * mm, "radius": 3.95 * mm, "construction": true});
            skLineSegment(sketch, "E80.0", {"start": v(2.05, 22.72) * mm, "end": v(2.05, 27.28) * mm});
            skLineSegment(sketch, "E80.1", {"start": v(2.05, 27.28) * mm, "end": v(6, 29.56) * mm});
            skLineSegment(sketch, "E80.2", {"start": v(6, 29.56) * mm, "end": v(9.95, 27.28) * mm});
            skLineSegment(sketch, "E80.3", {"start": v(9.95, 27.28) * mm, "end": v(9.95, 22.72) * mm});
            skLineSegment(sketch, "E80.4", {"start": v(9.95, 22.72) * mm, "end": v(6, 20.44) * mm});
            skLineSegment(sketch, "E80.5", {"start": v(6, 20.44) * mm, "end": v(2.05, 22.72) * mm});
            skPoint(sketch, "E80.0.midPoint", {"position": v(2.05, 25) * mm});
            skSolve(sketch);
        }
        {
            var Q0;
            Q0=makeQuery(id+"F37.imprint","IMPRINT",FACE,{"disambiguationData":[TD([[makeQuery(id+"F37.imprint","IMPRINT",EDGE,{"derivedFrom":sQuery(id+"F37.wireOp",EDGE,"E80.0")}),1.0]])]});
            var Q1;
            {var subQ0=sQuery(id+"F37.wireOp",EDGE,"E80.3");var subQ1=makeQuery(id+"F3.opExtrude","CAP_EDGE",EDGE,{"disambiguationData":[OSD([sQuery(id+"F2.wireOp",EDGE,"E7")])],"isStart":true});var subQ2=makeQuery(id+"F37.imprint","INTERSECT",VERTEX,{"disambiguationData":[OD(0.0)],"derivedFrom":[subQ1,subQ0]});Q1=makeQuery(id+"F37.imprint","IMPRINT",FACE,{"disambiguationData":[TD([[makeQuery(id+"F37.imprint","IMPRINT",EDGE,{"disambiguationData":[TD([[subQ2,-1.0]])],"derivedFrom":subQ0}),1.0]])]});}
            var Q2;
            {var subQ0=sQuery(id+"F0.wireOp",EDGE,"E0.top");var subQ3=sQuery(id+"F0.wireOp",EDGE,"E0.left");var subQ5=sQuery(id+"F0.wireOp",EDGE,"E4");var subQ6=sQuery(id+"F0.wireOp",EDGE,"E3");var subQ7=sQuery(id+"F0.wireOp",EDGE,"E1");var subQ8=sQuery(id+"F0.wireOp",EDGE,"E0.bottom");var subQ9=sQuery(id+"F0.wireOp",EDGE,"E0.right");Q2=makeQuery(id+"F9.boolean.opBoolean","SPLIT",FACE,{"disambiguationData":[TD([makeQuery(id+"F9.opExtrude","SWEPT_FACE",FACE,{"disambiguationData":[OSD([sQuery(id+"F8.wireOp",EDGE,"E37.right")])]})])],"derivedFrom":makeQuery(id+"F3.boolean.opBoolean","SPLIT",FACE,{"disambiguationData":[TD([makeQuery(id+"F1.opExtrude","SWEPT_FACE",FACE,{"disambiguationData":[OSD([subQ8])]})])],"derivedFrom":makeQuery(id+"F1.opExtrude","CAP_FACE",FACE,{"disambiguationData":[OSD([subQ8,subQ0,subQ3,subQ9,subQ7,subQ6,subQ5])],"isStart":false})})});}
            var Q3;
            {var subQ1=sQuery(id+"F0.wireOp",EDGE,"E0.bottom");var subQ2=makeQuery(id+"F1.opExtrude","SWEPT_FACE",FACE,{"disambiguationData":[OSD([subQ1])]});var subQ3=sQuery(id+"F0.wireOp",EDGE,"E0.left");var subQ5=sQuery(id+"F0.wireOp",EDGE,"E4");var subQ6=sQuery(id+"F0.wireOp",EDGE,"E3");var subQ7=sQuery(id+"F0.wireOp",EDGE,"E1");var subQ8=sQuery(id+"F0.wireOp",EDGE,"E0.right");var subQ9=sQuery(id+"F0.wireOp",EDGE,"E0.top");Q3=makeQuery(id+"F9.boolean.opBoolean","SPLIT",FACE,{"disambiguationData":[TD([makeQuery(id+"F9.opExtrude","SWEPT_FACE",FACE,{"disambiguationData":[OSD([sQuery(id+"F8.wireOp",EDGE,"E39.right")])]})])],"derivedFrom":makeQuery(id+"F3.boolean.opBoolean","SPLIT",FACE,{"disambiguationData":[TD([subQ2])],"derivedFrom":makeQuery(id+"F1.opExtrude","CAP_FACE",FACE,{"disambiguationData":[OSD([subQ1,subQ9,subQ3,subQ8,subQ7,subQ6,subQ5])],"isStart":false})})});}
            var Q4;
            {var subQ0=makeQuery(id+"F3.opExtrude","SWEPT_FACE",FACE,{"disambiguationData":[OSD([sQuery(id+"F2.wireOp",EDGE,"E5.right")])]});var subQ1=sQuery(id+"F0.wireOp",EDGE,"E0.right");var subQ3=sQuery(id+"F0.wireOp",EDGE,"E0.left");var subQ4=sQuery(id+"F0.wireOp",EDGE,"E4");var subQ5=sQuery(id+"F0.wireOp",EDGE,"E3");var subQ6=sQuery(id+"F0.wireOp",EDGE,"E1");var subQ7=sQuery(id+"F0.wireOp",EDGE,"E0.bottom");var subQ8=sQuery(id+"F0.wireOp",EDGE,"E0.top");Q4=makeQuery(id+"F9.boolean.opBoolean","SPLIT",FACE,{"disambiguationData":[TD([subQ0])],"derivedFrom":makeQuery(id+"F3.boolean.opBoolean","SPLIT",FACE,{"disambiguationData":[TD([makeQuery(id+"F1.opExtrude","SWEPT_FACE",FACE,{"disambiguationData":[OSD([subQ7])]})])],"derivedFrom":makeQuery(id+"F1.opExtrude","CAP_FACE",FACE,{"disambiguationData":[OSD([subQ7,subQ8,subQ3,subQ1,subQ6,subQ5,subQ4])],"isStart":false})})});}
            var Q5;
            Q5=makeQuery(id+"F36.imprint","IMPRINT",FACE,{"disambiguationData":[TD([[makeQuery(id+"F36.imprint","IMPRINT",EDGE,{"derivedFrom":sQuery(id+"F36.wireOp",EDGE,"E77.0")}),1.0]])]});
            extrude(context, id + "F38", {"entities" : qUnion([Q0, Q1, Q2, Q3, Q4, Q5]), "operationType" : NewBodyOperationType.ADD, "depth" : 2.5 * mm});
        }
        {
            var Q0;
            {var subQ0=sQuery(id+"F0.wireOp",EDGE,"E0.right");var subQ1=sQuery(id+"F0.wireOp",EDGE,"E0.bottom");var subQ2=makeQuery(id+"F1.opExtrude","SWEPT_FACE",FACE,{"disambiguationData":[OSD([subQ1])]});var subQ4=sQuery(id+"F0.wireOp",EDGE,"E3");var subQ5=makeQuery(id+"F1.opExtrude","SWEPT_FACE",FACE,{"disambiguationData":[OSD([subQ4])]});var subQ7=sQuery(id+"F0.wireOp",EDGE,"E0.left");var subQ8=sQuery(id+"F0.wireOp",EDGE,"E4");var subQ9=sQuery(id+"F0.wireOp",EDGE,"E1");var subQ10=sQuery(id+"F0.wireOp",EDGE,"E0.top");Q0=makeQuery(id+"F9.boolean.opBoolean","SPLIT",FACE,{"disambiguationData":[TD([subQ5])],"derivedFrom":makeQuery(id+"F3.boolean.opBoolean","SPLIT",FACE,{"disambiguationData":[TD([subQ2])],"derivedFrom":makeQuery(id+"F1.opExtrude","CAP_FACE",FACE,{"disambiguationData":[OSD([subQ1,subQ10,subQ7,subQ0,subQ9,subQ4,subQ8])],"isStart":false})})});}
            var sketch = newSketch(context, id + "F39", { "sketchPlane" : qUnion([Q0])});
            skCircle(sketch, "E81.cCircle", {"center": v(58, 6) * mm, "radius": 3.95 * mm, "construction": true});
            skLineSegment(sketch, "E81.0", {"start": v(61.95, 8.28) * mm, "end": v(61.95, 3.72) * mm});
            skLineSegment(sketch, "E81.1", {"start": v(61.95, 3.72) * mm, "end": v(58, 1.44) * mm});
            skLineSegment(sketch, "E81.2", {"start": v(58, 1.44) * mm, "end": v(54.05, 3.72) * mm});
            skLineSegment(sketch, "E81.3", {"start": v(54.05, 3.72) * mm, "end": v(54.05, 8.28) * mm});
            skLineSegment(sketch, "E81.4", {"start": v(54.05, 8.28) * mm, "end": v(58, 10.56) * mm});
            skLineSegment(sketch, "E81.5", {"start": v(58, 10.56) * mm, "end": v(61.95, 8.28) * mm});
            skPoint(sketch, "E81.0.midPoint", {"position": v(61.95, 6) * mm});
            skSolve(sketch);
        }
        {
            var Q0;
            Q0=makeQuery(id+"F39.imprint","IMPRINT",FACE,{"disambiguationData":[TD([[makeQuery(id+"F39.imprint","IMPRINT",EDGE,{"derivedFrom":sQuery(id+"F39.wireOp",EDGE,"E81.0")}),1.0]])]});
            extrude(context, id + "F40", {"entities" : qUnion([Q0]), "operationType" : NewBodyOperationType.ADD, "depth" : 2.5 * mm});
        }
        {
            var Q0;
            {var subQ0=makeQuery(id+"F3.opExtrude","SWEPT_FACE",FACE,{"disambiguationData":[OSD([sQuery(id+"F2.wireOp",EDGE,"E5.right")])]});var subQ1=sQuery(id+"F0.wireOp",EDGE,"E0.right");var subQ3=sQuery(id+"F0.wireOp",EDGE,"E0.left");var subQ4=sQuery(id+"F0.wireOp",EDGE,"E4");var subQ5=sQuery(id+"F0.wireOp",EDGE,"E3");var subQ6=sQuery(id+"F0.wireOp",EDGE,"E1");var subQ7=sQuery(id+"F0.wireOp",EDGE,"E0.bottom");var subQ8=sQuery(id+"F0.wireOp",EDGE,"E0.top");Q0=makeQuery(id+"F38.opExtrude","CAP_FACE",FACE,{"disambiguationData":[OSD([subQ7,subQ8,subQ3,subQ1,subQ6,subQ5,subQ4]),TDD([makeQuery(id+"F9.boolean.opBoolean","SPLIT",FACE,{"disambiguationData":[TD([subQ0])],"derivedFrom":makeQuery(id+"F3.boolean.opBoolean","SPLIT",FACE,{"disambiguationData":[TD([makeQuery(id+"F1.opExtrude","SWEPT_FACE",FACE,{"disambiguationData":[OSD([subQ7])]})])],"derivedFrom":makeQuery(id+"F1.opExtrude","CAP_FACE",FACE,{"disambiguationData":[OSD([subQ7,subQ8,subQ3,subQ1,subQ6,subQ5,subQ4])],"isStart":false})})})])],"isStart":false});}
            var sketch = newSketch(context, id + "F41", { "sketchPlane" : qUnion([Q0])});
            skLineSegment(sketch, "E82.0.0", {"start": v(0, 35.15) * mm, "end": v(1.12, 35.15) * mm});
            skLineSegment(sketch, "E82.0.1", {"start": v(1.12, 35.15) * mm, "end": v(7.85, 35.15) * mm});
            skLineSegment(sketch, "E82.0.2", {"start": v(7.85, 35.15) * mm, "end": v(7.85, 39.15) * mm});
            skLineSegment(sketch, "E82.0.3", {"start": v(7.85, 39.15) * mm, "end": v(1.12, 39.15) * mm});
            skLineSegment(sketch, "E82.0.4", {"start": v(1.12, 39.15) * mm, "end": v(0, 39.15) * mm});
            skLineSegment(sketch, "E82.0.5", {"start": v(0, 39.15) * mm, "end": v(0, 35.15) * mm});
            skLineSegment(sketch, "E83.0.0", {"start": v(56.15, 35.15) * mm, "end": v(62.88, 35.15) * mm});
            skLineSegment(sketch, "E83.0.1", {"start": v(62.88, 35.15) * mm, "end": v(64, 35.15) * mm});
            skLineSegment(sketch, "E83.0.2", {"start": v(64, 35.15) * mm, "end": v(64, 39.15) * mm});
            skLineSegment(sketch, "E83.0.3", {"start": v(64, 39.15) * mm, "end": v(62.88, 39.15) * mm});
            skLineSegment(sketch, "E83.0.4", {"start": v(62.88, 39.15) * mm, "end": v(56.15, 39.15) * mm});
            skLineSegment(sketch, "E83.0.5", {"start": v(56.15, 39.15) * mm, "end": v(56.15, 35.15) * mm});
            skLineSegment(sketch, "E84.0.0", {"start": v(56.15, 14.85) * mm, "end": v(56.15, 10.85) * mm});
            skLineSegment(sketch, "E84.0.1", {"start": v(56.15, 10.85) * mm, "end": v(62.88, 10.85) * mm});
            skLineSegment(sketch, "E84.0.2", {"start": v(62.88, 10.85) * mm, "end": v(64, 10.85) * mm});
            skLineSegment(sketch, "E84.0.3", {"start": v(64, 10.85) * mm, "end": v(64, 14.85) * mm});
            skLineSegment(sketch, "E84.0.4", {"start": v(64, 14.85) * mm, "end": v(62.88, 14.85) * mm});
            skLineSegment(sketch, "E84.0.5", {"start": v(62.88, 14.85) * mm, "end": v(56.15, 14.85) * mm});
            skLineSegment(sketch, "E85.0.0", {"start": v(0, 14.85) * mm, "end": v(0, 10.85) * mm});
            skLineSegment(sketch, "E85.0.1", {"start": v(0, 10.85) * mm, "end": v(1.12, 10.85) * mm});
            skLineSegment(sketch, "E85.0.2", {"start": v(1.12, 10.85) * mm, "end": v(7.85, 10.85) * mm});
            skLineSegment(sketch, "E85.0.3", {"start": v(7.85, 10.85) * mm, "end": v(7.85, 14.85) * mm});
            skLineSegment(sketch, "E85.0.4", {"start": v(7.85, 14.85) * mm, "end": v(1.12, 14.85) * mm});
            skLineSegment(sketch, "E85.0.5", {"start": v(1.12, 14.85) * mm, "end": v(0, 14.85) * mm});
            skSolve(sketch);
        }
        {
            var Q0;
            Q0 = qSketchRegion(id + "F41", true);
            extrude(context, id + "F42", {"entities" : qUnion([Q0]), "operationType" : NewBodyOperationType.ADD, "endBound" : BoundingType.UP_TO_NEXT, "oppositeDirection" : true, "depth" : 25 * mm});
        }
        {
            var Q0;
            {var subQ1=sQuery(id+"F0.wireOp",EDGE,"E0.left");var subQ7=makeQuery(id+"F1.opExtrude","CAP_EDGE",EDGE,{"disambiguationData":[OSD([subQ1])],"isStart":false});Q0=makeQuery(id+"F42.boolean.opBoolean","MERGE",EDGE,{"derivedFrom":[makeQuery(id+"F38.opExtrude","CAP_EDGE",EDGE,{"disambiguationData":[OSD([subQ1]),TDD([makeQuery(id+"F9.boolean.opBoolean","SPLIT",EDGE,{"disambiguationData":[TD([makeQuery(id+"F3.opExtrude","SWEPT_FACE",FACE,{"disambiguationData":[OSD([sQuery(id+"F2.wireOp",EDGE,"E5.top")])]})])],"derivedFrom":subQ7})])],"isStart":false}),makeQuery(id+"F38.opExtrude","CAP_EDGE",EDGE,{"disambiguationData":[OSD([subQ1]),TDD([makeQuery(id+"F9.boolean.opBoolean","SPLIT",EDGE,{"disambiguationData":[TD([makeQuery(id+"F3.opExtrude","SWEPT_FACE",FACE,{"disambiguationData":[OSD([sQuery(id+"F2.wireOp",EDGE,"E5.bottom")])]})])],"derivedFrom":subQ7})])],"isStart":false}),makeQuery(id+"F38.opExtrude","CAP_EDGE",EDGE,{"disambiguationData":[OSD([subQ1]),TDD([makeQuery(id+"F37.imprint","IMPRINT",EDGE,{"derivedFrom":makeQuery(id+"F9.boolean.opBoolean","SPLIT",EDGE,{"disambiguationData":[TD([makeQuery(id+"F9.opExtrude","SWEPT_FACE",FACE,{"disambiguationData":[OSD([sQuery(id+"F8.wireOp",EDGE,"E27.top")])]})])],"derivedFrom":subQ7})})])],"isStart":false}),makeQuery(id+"F42.opExtrude","CAP_EDGE",EDGE,{"disambiguationData":[OSD([sQuery(id+"F41.wireOp",EDGE,"E82.0.5")])],"isStart":true}),makeQuery(id+"F42.opExtrude","CAP_EDGE",EDGE,{"disambiguationData":[OSD([sQuery(id+"F41.wireOp",EDGE,"E85.0.0")])],"isStart":true})]});}
            var Q1;
            {var subQ0=sQuery(id+"F0.wireOp",EDGE,"E0.left");var subQ1=sQuery(id+"F0.wireOp",EDGE,"E4");var subQ2=sQuery(id+"F0.wireOp",EDGE,"E3");var subQ3=sQuery(id+"F0.wireOp",EDGE,"E1");var subQ4=sQuery(id+"F0.wireOp",EDGE,"E0.bottom");var subQ5=sQuery(id+"F0.wireOp",EDGE,"E0.right");var subQ6=sQuery(id+"F0.wireOp",EDGE,"E0.top");Q1=makeQuery(id+"F38.opExtrude","CAP_EDGE",EDGE,{"disambiguationData":[OSD([subQ4,subQ6,subQ0,subQ5,subQ3,subQ2,subQ1]),TDD([makeQuery(id+"F36.imprint","IMPRINT",EDGE,{"derivedFrom":makeQuery(id+"F7.opFillet","BLEND_EDGE",EDGE,{"blendedFrom":[makeQuery(id+"F1.opExtrude","SWEPT_EDGE",EDGE,{"disambiguationData":[OSD([subQ6,subQ5])]}),makeQuery(id+"F3.boolean.opBoolean","SPLIT",FACE,{"disambiguationData":[TD([makeQuery(id+"F1.opExtrude","SWEPT_FACE",FACE,{"disambiguationData":[OSD([subQ4])]})])],"derivedFrom":makeQuery(id+"F1.opExtrude","CAP_FACE",FACE,{"disambiguationData":[OSD([subQ4,subQ6,subQ0,subQ5,subQ3,subQ2,subQ1])],"isStart":false})})],"blendedInto":[makeQuery(id+"F3.boolean.opBoolean","SPLIT",FACE,{"disambiguationData":[TD([makeQuery(id+"F1.opExtrude","SWEPT_FACE",FACE,{"disambiguationData":[OSD([subQ4])]})])],"derivedFrom":makeQuery(id+"F1.opExtrude","CAP_FACE",FACE,{"disambiguationData":[OSD([subQ4,subQ6,subQ0,subQ5,subQ3,subQ2,subQ1])],"isStart":false})})]})})])],"isStart":false});}
            chamfer(context, id + "F43", {"entities" : qUnion([Q0, Q1]), "width" : 1 * mm, "tangentPropagation" : true});
        }
        {
            var Q0;
            {var subQ2=sQuery(id+"F2.wireOp",EDGE,"E5.top");Q0=makeQuery(id+"F42.boolean.opBoolean","INTERSECT",EDGE,{"derivedFrom":[makeQuery(id+"F11.boolean.opBoolean","COPY",FACE,{"disambiguationData":[TD([makeQuery(id+"F3.opExtrude","SWEPT_FACE",FACE,{"disambiguationData":[OSD([subQ2])]})])],"derivedFrom":makeQuery(id+"F11.opExtrude","SWEPT_FACE",FACE,{"disambiguationData":[OSD([sQuery(id+"F10.wireOp",EDGE,"E47")])]})}),makeQuery(id+"F42.opExtrude","CAP_FACE",FACE,{"disambiguationData":[OSD([sQuery(id+"F41.wireOp",EDGE,"E85.0.0"),sQuery(id+"F41.wireOp",EDGE,"E85.0.1"),sQuery(id+"F41.wireOp",EDGE,"E85.0.2"),sQuery(id+"F41.wireOp",EDGE,"E85.0.3"),sQuery(id+"F41.wireOp",EDGE,"E85.0.4"),sQuery(id+"F41.wireOp",EDGE,"E85.0.5")])],"isStart":true})]});}
            var Q1;
            {var subQ4=sQuery(id+"F2.wireOp",EDGE,"E5.bottom");Q1=makeQuery(id+"F42.boolean.opBoolean","INTERSECT",EDGE,{"derivedFrom":[makeQuery(id+"F11.boolean.opBoolean","COPY",FACE,{"disambiguationData":[TD([makeQuery(id+"F3.opExtrude","SWEPT_FACE",FACE,{"disambiguationData":[OSD([subQ4])]})])],"derivedFrom":makeQuery(id+"F11.opExtrude","SWEPT_FACE",FACE,{"disambiguationData":[OSD([sQuery(id+"F10.wireOp",EDGE,"E47")])]})}),makeQuery(id+"F42.opExtrude","CAP_FACE",FACE,{"disambiguationData":[OSD([sQuery(id+"F41.wireOp",EDGE,"E82.0.0"),sQuery(id+"F41.wireOp",EDGE,"E82.0.1"),sQuery(id+"F41.wireOp",EDGE,"E82.0.2"),sQuery(id+"F41.wireOp",EDGE,"E82.0.3"),sQuery(id+"F41.wireOp",EDGE,"E82.0.4"),sQuery(id+"F41.wireOp",EDGE,"E82.0.5")])],"isStart":true})]});}
            var Q2;
            {var subQ4=sQuery(id+"F2.wireOp",EDGE,"E5.bottom");Q2=makeQuery(id+"F42.boolean.opBoolean","INTERSECT",EDGE,{"derivedFrom":[makeQuery(id+"F11.boolean.opBoolean","COPY",FACE,{"disambiguationData":[TD([makeQuery(id+"F3.opExtrude","SWEPT_FACE",FACE,{"disambiguationData":[OSD([subQ4])]})])],"derivedFrom":makeQuery(id+"F11.opExtrude","SWEPT_FACE",FACE,{"disambiguationData":[OSD([sQuery(id+"F10.wireOp",EDGE,"E44")])]})}),makeQuery(id+"F42.opExtrude","CAP_FACE",FACE,{"disambiguationData":[OSD([sQuery(id+"F41.wireOp",EDGE,"E83.0.0"),sQuery(id+"F41.wireOp",EDGE,"E83.0.1"),sQuery(id+"F41.wireOp",EDGE,"E83.0.2"),sQuery(id+"F41.wireOp",EDGE,"E83.0.3"),sQuery(id+"F41.wireOp",EDGE,"E83.0.4"),sQuery(id+"F41.wireOp",EDGE,"E83.0.5")])],"isStart":true})]});}
            var Q3;
            {var subQ0=sQuery(id+"F2.wireOp",EDGE,"E5.top");Q3=makeQuery(id+"F42.boolean.opBoolean","INTERSECT",EDGE,{"derivedFrom":[makeQuery(id+"F11.boolean.opBoolean","COPY",FACE,{"disambiguationData":[TD([makeQuery(id+"F3.opExtrude","SWEPT_FACE",FACE,{"disambiguationData":[OSD([subQ0])]})])],"derivedFrom":makeQuery(id+"F11.opExtrude","SWEPT_FACE",FACE,{"disambiguationData":[OSD([sQuery(id+"F10.wireOp",EDGE,"E44")])]})}),makeQuery(id+"F42.opExtrude","CAP_FACE",FACE,{"disambiguationData":[OSD([sQuery(id+"F41.wireOp",EDGE,"E84.0.0"),sQuery(id+"F41.wireOp",EDGE,"E84.0.1"),sQuery(id+"F41.wireOp",EDGE,"E84.0.2"),sQuery(id+"F41.wireOp",EDGE,"E84.0.3"),sQuery(id+"F41.wireOp",EDGE,"E84.0.4"),sQuery(id+"F41.wireOp",EDGE,"E84.0.5")])],"isStart":true})]});}
            fillet(context, id + "F44", {"entities" : qUnion([Q0, Q1, Q2, Q3]), "radius" : 5 * mm, "tangentPropagation" : true, "allowEdgeOverflow" : false});
        }
        {
            var Q0;
            Q0=makeQuery(id+"F9.boolean.opBoolean","MERGE",EDGE,{"disambiguationData":[OD(2.0)],"derivedFrom":[makeQuery(id+"F3.opExtrude","CAP_EDGE",EDGE,{"disambiguationData":[OSD([sQuery(id+"F2.wireOp",EDGE,"E5.top")])],"isStart":true}),makeQuery(id+"F9.opExtrude","CAP_EDGE",EDGE,{"disambiguationData":[OSD([sQuery(id+"F8.wireOp",EDGE,"E28.bottom")])],"isStart":true}),makeQuery(id+"F9.opExtrude","CAP_EDGE",EDGE,{"disambiguationData":[OSD([sQuery(id+"F8.wireOp",EDGE,"E30.bottom")])],"isStart":true})]});
            var Q1;
            Q1=makeQuery(id+"F9.boolean.opBoolean","MERGE",EDGE,{"disambiguationData":[OD(2.0)],"derivedFrom":[makeQuery(id+"F3.opExtrude","CAP_EDGE",EDGE,{"disambiguationData":[OSD([sQuery(id+"F2.wireOp",EDGE,"E5.bottom")])],"isStart":true}),makeQuery(id+"F9.opExtrude","CAP_EDGE",EDGE,{"disambiguationData":[OSD([sQuery(id+"F8.wireOp",EDGE,"E27.bottom")])],"isStart":true}),makeQuery(id+"F9.opExtrude","CAP_EDGE",EDGE,{"disambiguationData":[OSD([sQuery(id+"F8.wireOp",EDGE,"E29.bottom")])],"isStart":true})]});
            fillet(context, id + "F45", {"entities" : qUnion([Q0, Q1]), "radius" : 5 * mm, "tangentPropagation" : true, "allowEdgeOverflow" : false});
        }
    });
